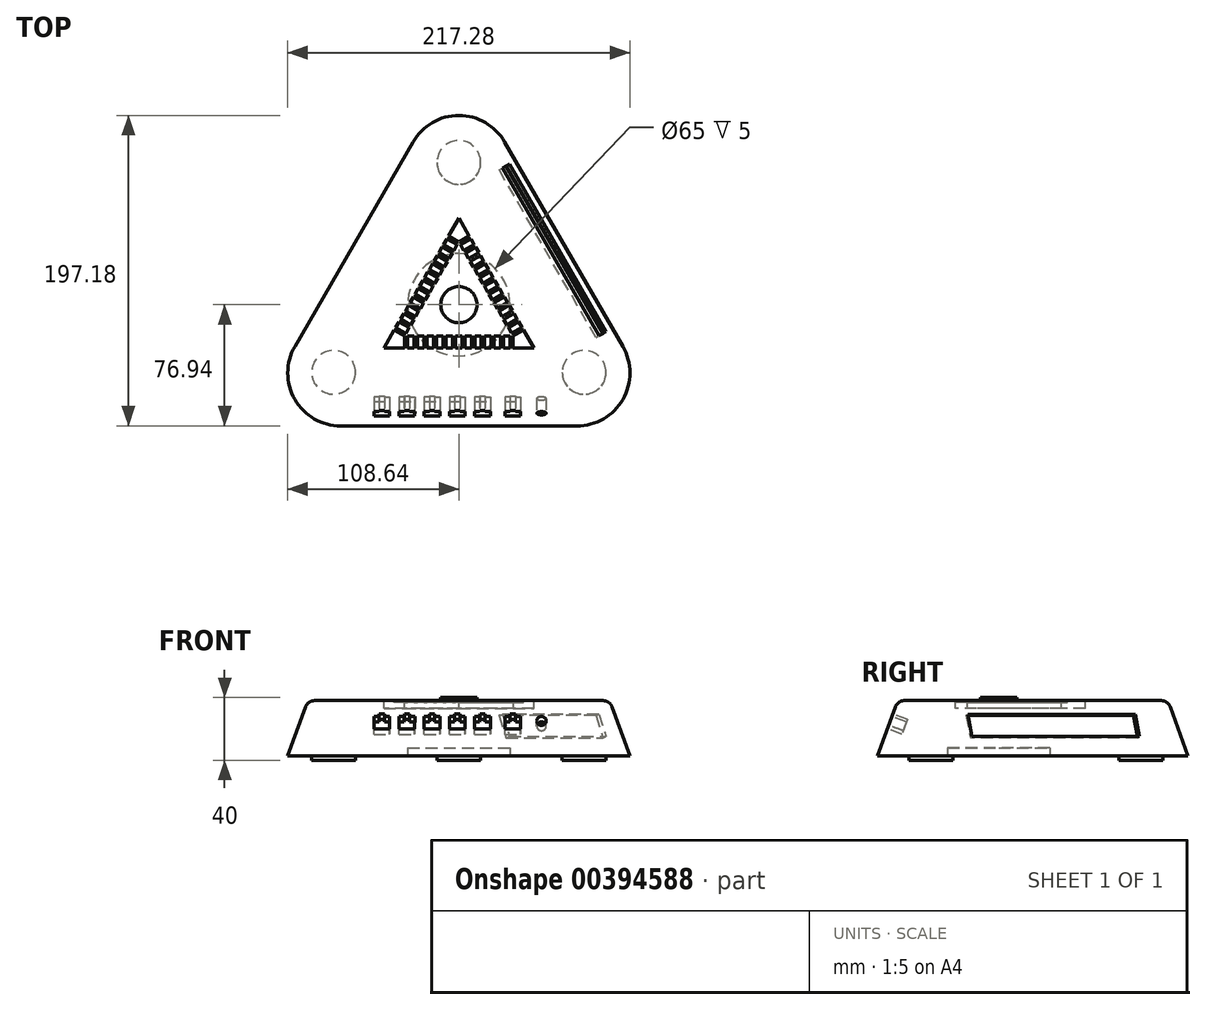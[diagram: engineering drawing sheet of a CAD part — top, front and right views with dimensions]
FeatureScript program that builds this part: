
annotation { "Feature Type Name" : "Feature", "Feature Type Description" : "" }
export const myFeature = defineFeature(function(context is Context, id is Id, definition is map)
    precondition{}
    {
        {
            var Q0;
            Q0=qCreatedBy(makeId("Top.planeOp"),FACE);
            var sketch = newSketch(context, id + "F0", { "sketchPlane" : qUnion([Q0])});
            skCircle(sketch, "E0.cCircle", {"center": v(0, 0) * mm, "radius": 73.3 * mm, "construction": true});
            skLineSegment(sketch, "E0.0", {"start": v(75, -73.3) * mm, "end": v(-75, -73.3) * mm});
            skLineSegment(sketch, "E0.1", {"start": v(-100.98, -28.3) * mm, "end": v(-25.98, 101.6) * mm});
            skLineSegment(sketch, "E0.2", {"start": v(25.98, 101.6) * mm, "end": v(100.98, -28.3) * mm});
            skPoint(sketch, "E0.0.midPoint", {"position": v(0, -73.3) * mm});
            skPoint(sketch, "E1.visualSharp", {"position": v(0, 146.6) * mm});
            skArc(sketch, "E1.filletArc", {"start": v(25.98, 101.6) * mm, "mid": v(0, 116.6) * mm, "end": v(-25.98, 101.6) * mm});
            skPoint(sketch, "E2.visualSharp", {"position": v(126.96, -73.3) * mm});
            skArc(sketch, "E2.filletArc", {"start": v(75, -73.3) * mm, "mid": v(100.98, -58.3) * mm, "end": v(100.98, -28.3) * mm});
            skPoint(sketch, "E3.visualSharp", {"position": v(-126.96, -73.3) * mm});
            skArc(sketch, "E3.filletArc", {"start": v(-100.98, -28.3) * mm, "mid": v(-100.98, -58.3) * mm, "end": v(-75, -73.3) * mm});
            skSolve(sketch);
        }
        {
            var Q0;
            Q0=makeQuery(id+"F0.imprint","IMPRINT",FACE,{"disambiguationData":[TD([[makeQuery(id+"F0.imprint","IMPRINT",EDGE,{"derivedFrom":sQuery(id+"F0.wireOp",EDGE,"E0.0")}),-1.0]])]});
            extrude(context, id + "F1", {"entities" : qUnion([Q0]), "depth" : 25 * mm, "hasDraft" : true, "draftAngle" : 20 * degree, "draftPullDirection" : true, "hasSecondDirection" : true, "secondDirectionOppositeDirection" : true, "secondDirectionDepth" : 10 * mm, "hasSecondDirectionDraft" : true, "secondDirectionDraftAngle" : 20 * degree});
        }
        {
            var Q0;
            Q0=makeQuery(id+"F1.opExtrude","CAP_EDGE",EDGE,{"disambiguationData":[OSD([sQuery(id+"F0.wireOp",EDGE,"E0.0")])],"isStart":false});
            var Q1;
            Q1=makeQuery(id+"F1.opExtrude","CAP_EDGE",EDGE,{"disambiguationData":[OSD([sQuery(id+"F0.wireOp",EDGE,"E0.2")])],"isStart":false});
            var Q2;
            Q2=makeQuery(id+"F1.opExtrude","CAP_EDGE",EDGE,{"disambiguationData":[OSD([sQuery(id+"F0.wireOp",EDGE,"E0.1")])],"isStart":false});
            fillet(context, id + "F2", {"entities" : qUnion([Q0, Q1, Q2]), "radius" : 6 * mm, "tangentPropagation" : true, "allowEdgeOverflow" : false});
        }
        {
            var Q0;
            Q0=makeQuery(id+"F1.opExtrude","CAP_FACE",FACE,{"disambiguationData":[OSD([sQuery(id+"F0.wireOp",EDGE,"E0.0"),sQuery(id+"F0.wireOp",EDGE,"E0.1"),sQuery(id+"F0.wireOp",EDGE,"E0.2"),sQuery(id+"F0.wireOp",EDGE,"E1.filletArc"),sQuery(id+"F0.wireOp",EDGE,"E2.filletArc"),sQuery(id+"F0.wireOp",EDGE,"E3.filletArc")])],"isStart":false});
            var sketch = newSketch(context, id + "F3", { "sketchPlane" : qUnion([Q0])});
            skCircle(sketch, "E4", {"center": v(0, 0) * mm, "radius": 11.5 * mm});
            skCircle(sketch, "E5.cCircle", {"center": v(0, 0) * mm, "radius": 20 * mm, "construction": true});
            skLineSegment(sketch, "E5.0", {"start": v(34.64, -20) * mm, "end": v(-34.64, -20) * mm});
            skLineSegment(sketch, "E5.1", {"start": v(-34.64, -20) * mm, "end": v(0, 40) * mm});
            skLineSegment(sketch, "E5.2", {"start": v(0, 40) * mm, "end": v(34.64, -20) * mm});
            skPoint(sketch, "E5.0.midPoint", {"position": v(0, -20) * mm});
            skCircle(sketch, "E6.cCircle", {"center": v(0, 0) * mm, "radius": 27.5 * mm, "construction": true});
            skLineSegment(sketch, "E6.0", {"start": v(47.63, -27.5) * mm, "end": v(-47.63, -27.5) * mm});
            skLineSegment(sketch, "E6.1", {"start": v(-47.63, -27.5) * mm, "end": v(0, 55) * mm});
            skLineSegment(sketch, "E6.2", {"start": v(0, 55) * mm, "end": v(47.63, -27.5) * mm});
            skPoint(sketch, "E6.0.midPoint", {"position": v(0, -27.5) * mm});
            skSolve(sketch);
        }
        {
            var Q0;
            Q0=makeQuery(id+"F3.imprint","IMPRINT",FACE,{"disambiguationData":[TD([[makeQuery(id+"F3.imprint","IMPRINT",EDGE,{"derivedFrom":sQuery(id+"F3.wireOp",EDGE,"E4")}),1.0]])]});
            extrude(context, id + "F4", {"entities" : qUnion([Q0]), "operationType" : NewBodyOperationType.ADD, "depth" : 2 * mm});
        }
        {
            var Q0;
            Q0=makeQuery(id+"F4.opExtrude","CAP_FACE",FACE,{"disambiguationData":[OSD([sQuery(id+"F3.wireOp",EDGE,"E4")])],"isStart":false});
            var sketch = newSketch(context, id + "F5", { "sketchPlane" : qUnion([Q0])});
            skSolve(sketch);
        }
        {
            var Q0;
            Q0=makeQuery(id+"F1.opExtrude","CAP_FACE",FACE,{"disambiguationData":[OSD([sQuery(id+"F0.wireOp",EDGE,"E0.0"),sQuery(id+"F0.wireOp",EDGE,"E0.1"),sQuery(id+"F0.wireOp",EDGE,"E0.2"),sQuery(id+"F0.wireOp",EDGE,"E1.filletArc"),sQuery(id+"F0.wireOp",EDGE,"E2.filletArc"),sQuery(id+"F0.wireOp",EDGE,"E3.filletArc")])],"isStart":true});
            var sketch = newSketch(context, id + "F6", { "sketchPlane" : qUnion([Q0])});
            skPoint(sketch, "E7.orphan", {"position": v(0, 0) * mm});
            skPoint(sketch, "E8.orphan", {"position": v(-104.13, 60.12) * mm});
            skPoint(sketch, "E9.end.orphan", {"position": v(0, -120.24) * mm});
            skCircle(sketch, "E10", {"center": v(-79.56, 42.91) * mm, "radius": 13.93 * mm});
            skLineSegment(sketch, "E11", {"start": v(0, 0) * mm, "end": v(66.63, -38.47) * mm});
            skCircle(sketch, "E12.MirrorC", {"center": v(79.56, 42.91) * mm, "radius": 13.93 * mm});
            skCircle(sketch, "E13.MirrorC", {"center": v(0, -90.36) * mm, "radius": 13.93 * mm});
            skPoint(sketch, "E14.end.orphan", {"position": v(-66.63, -38.47) * mm});
            skPoint(sketch, "E15.end.orphan", {"position": v(0, 76.94) * mm});
            skCircle(sketch, "E16.cCircle", {"center": v(0, 0) * mm, "radius": 30 * mm, "construction": true});
            skPoint(sketch, "E16.0.midPoint", {"position": v(0, 30) * mm});
            skSolve(sketch);
        }
        {
            var Q0;
            Q0=qSketchRegion(id+"F6",true);
            extrude(context, id + "F7", {"entities" : qUnion([Q0]), "operationType" : NewBodyOperationType.ADD, "depth" : 3 * mm});
        }
        {
            var Q0;
            Q0=makeQuery(id+"F1.opExtrude","CAP_FACE",FACE,{"disambiguationData":[OSD([sQuery(id+"F0.wireOp",EDGE,"E0.0"),sQuery(id+"F0.wireOp",EDGE,"E0.1"),sQuery(id+"F0.wireOp",EDGE,"E0.2"),sQuery(id+"F0.wireOp",EDGE,"E1.filletArc"),sQuery(id+"F0.wireOp",EDGE,"E2.filletArc"),sQuery(id+"F0.wireOp",EDGE,"E3.filletArc")])],"isStart":true});
            var sketch = newSketch(context, id + "F8", { "sketchPlane" : qUnion([Q0])});
            skCircle(sketch, "E17", {"center": v(0, 0) * mm, "radius": 32.5 * mm});
            skSolve(sketch);
        }
        {
            var Q0;
            Q0=qSketchRegion(id+"F8",true);
            extrude(context, id + "F9", {"entities" : qUnion([Q0]), "operationType" : NewBodyOperationType.REMOVE, "oppositeDirection" : true, "depth" : 5 * mm});
        }
        {
            var Q0;
            Q0=makeQuery(id+"F1.*.split.splitOp","SPLIT",FACE,{"derivedFrom":makeQuery(id+"F1.opExtrude","SWEPT_FACE",FACE,{"disambiguationData":[OSD([sQuery(id+"F0.wireOp",EDGE,"E0.0")])]})});
            var sketch = newSketch(context, id + "F10", { "sketchPlane" : qUnion([Q0])});
            skLineSegment(sketch, "E18.top", {"start": v(-53.99, -17.5) * mm, "end": v(-43.99, -17.5) * mm});
            skLineSegment(sketch, "E19", {"start": v(-53.99, -9.3) * mm, "end": v(-53.99, -17.5) * mm});
            skLineSegment(sketch, "E20", {"start": v(-43.96, -9.24) * mm, "end": v(-43.99, -17.5) * mm});
            skLineSegment(sketch, "E21", {"start": v(-50.6, -7.5) * mm, "end": v(-47.3, -7.5) * mm});
            skLineSegment(sketch, "E22", {"start": v(-50.6, -7.5) * mm, "end": v(-50.74, -9.3) * mm});
            skLineSegment(sketch, "E23", {"start": v(-50.74, -9.3) * mm, "end": v(-53.99, -9.3) * mm});
            skLineSegment(sketch, "E24", {"start": v(-47.3, -7.5) * mm, "end": v(-47.3, -9.3) * mm});
            skLineSegment(sketch, "E25", {"start": v(-47.3, -9.3) * mm, "end": v(-43.96, -9.24) * mm});
            skPoint(sketch, "E18.left.start.orphan", {"position": v(-53.99, -7.5) * mm});
            skPoint(sketch, "E18.right.start.orphan", {"position": v(-43.99, -7.5) * mm});
            skLineSegment(sketch, "E26.1.0.0", {"start": v(-37.99, -9.3) * mm, "end": v(-37.99, -17.5) * mm});
            skLineSegment(sketch, "E26.1.0.1", {"start": v(-27.96, -9.24) * mm, "end": v(-27.99, -17.5) * mm});
            skPoint(sketch, "E26.1.0.2", {"position": v(-37.99, -7.5) * mm});
            skPoint(sketch, "E26.1.0.3", {"position": v(-27.99, -7.5) * mm});
            skLineSegment(sketch, "E26.1.0.4", {"start": v(-37.99, -17.5) * mm, "end": v(-27.99, -17.5) * mm});
            skLineSegment(sketch, "E26.1.0.5", {"start": v(-34.6, -7.5) * mm, "end": v(-31.3, -7.5) * mm});
            skLineSegment(sketch, "E26.1.0.6", {"start": v(-31.3, -7.5) * mm, "end": v(-31.3, -9.3) * mm});
            skLineSegment(sketch, "E26.1.0.7", {"start": v(-34.6, -7.5) * mm, "end": v(-34.74, -9.3) * mm});
            skLineSegment(sketch, "E26.1.0.8", {"start": v(-34.74, -9.3) * mm, "end": v(-37.99, -9.3) * mm});
            skLineSegment(sketch, "E26.1.0.9", {"start": v(-31.3, -9.3) * mm, "end": v(-27.96, -9.24) * mm});
            skLineSegment(sketch, "E26.2.0.0", {"start": v(-21.99, -9.3) * mm, "end": v(-21.99, -17.5) * mm});
            skLineSegment(sketch, "E26.2.0.1", {"start": v(-11.96, -9.24) * mm, "end": v(-11.99, -17.5) * mm});
            skPoint(sketch, "E26.2.0.2", {"position": v(-21.99, -7.5) * mm});
            skPoint(sketch, "E26.2.0.3", {"position": v(-11.99, -7.5) * mm});
            skLineSegment(sketch, "E26.2.0.4", {"start": v(-21.99, -17.5) * mm, "end": v(-11.99, -17.5) * mm});
            skLineSegment(sketch, "E26.2.0.5", {"start": v(-18.6, -7.5) * mm, "end": v(-15.3, -7.5) * mm});
            skLineSegment(sketch, "E26.2.0.6", {"start": v(-15.3, -7.5) * mm, "end": v(-15.3, -9.3) * mm});
            skLineSegment(sketch, "E26.2.0.7", {"start": v(-18.6, -7.5) * mm, "end": v(-18.74, -9.3) * mm});
            skLineSegment(sketch, "E26.2.0.8", {"start": v(-18.74, -9.3) * mm, "end": v(-21.99, -9.3) * mm});
            skLineSegment(sketch, "E26.2.0.9", {"start": v(-15.3, -9.3) * mm, "end": v(-11.96, -9.24) * mm});
            skLineSegment(sketch, "E26.3.0.0", {"start": v(-5.99, -9.3) * mm, "end": v(-5.99, -17.5) * mm});
            skLineSegment(sketch, "E26.3.0.1", {"start": v(4.04, -9.24) * mm, "end": v(4.01, -17.5) * mm});
            skPoint(sketch, "E26.3.0.2", {"position": v(-5.99, -7.5) * mm});
            skPoint(sketch, "E26.3.0.3", {"position": v(4.01, -7.5) * mm});
            skLineSegment(sketch, "E26.3.0.4", {"start": v(-5.99, -17.5) * mm, "end": v(4.01, -17.5) * mm});
            skLineSegment(sketch, "E26.3.0.5", {"start": v(-2.6, -7.5) * mm, "end": v(0.7, -7.5) * mm});
            skLineSegment(sketch, "E26.3.0.6", {"start": v(0.7, -7.5) * mm, "end": v(0.7, -9.3) * mm});
            skLineSegment(sketch, "E26.3.0.7", {"start": v(-2.6, -7.5) * mm, "end": v(-2.74, -9.3) * mm});
            skLineSegment(sketch, "E26.3.0.8", {"start": v(-2.74, -9.3) * mm, "end": v(-5.99, -9.3) * mm});
            skLineSegment(sketch, "E26.3.0.9", {"start": v(0.7, -9.3) * mm, "end": v(4.04, -9.24) * mm});
            skLineSegment(sketch, "E26.4.0.0", {"start": v(10.01, -9.3) * mm, "end": v(10.01, -17.5) * mm});
            skLineSegment(sketch, "E26.4.0.1", {"start": v(20.04, -9.24) * mm, "end": v(20.01, -17.5) * mm});
            skPoint(sketch, "E26.4.0.2", {"position": v(10.01, -7.5) * mm});
            skPoint(sketch, "E26.4.0.3", {"position": v(20.01, -7.5) * mm});
            skLineSegment(sketch, "E26.4.0.4", {"start": v(10.01, -17.5) * mm, "end": v(20.01, -17.5) * mm});
            skLineSegment(sketch, "E26.4.0.5", {"start": v(13.4, -7.5) * mm, "end": v(16.7, -7.5) * mm});
            skLineSegment(sketch, "E26.4.0.6", {"start": v(16.7, -7.5) * mm, "end": v(16.7, -9.3) * mm});
            skLineSegment(sketch, "E26.4.0.7", {"start": v(13.4, -7.5) * mm, "end": v(13.26, -9.3) * mm});
            skLineSegment(sketch, "E26.4.0.8", {"start": v(13.26, -9.3) * mm, "end": v(10.01, -9.3) * mm});
            skLineSegment(sketch, "E26.4.0.9", {"start": v(16.7, -9.3) * mm, "end": v(20.04, -9.24) * mm});
            skLineSegment(sketch, "E26.5.0.0", {"start": v(29.26, -9.3) * mm, "end": v(29.26, -17.5) * mm});
            skLineSegment(sketch, "E26.5.0.1", {"start": v(39.3, -9.24) * mm, "end": v(39.26, -17.5) * mm});
            skPoint(sketch, "E26.5.0.2", {"position": v(29.26, -7.5) * mm});
            skPoint(sketch, "E26.5.0.3", {"position": v(39.26, -7.5) * mm});
            skLineSegment(sketch, "E26.5.0.4", {"start": v(29.26, -17.5) * mm, "end": v(39.26, -17.5) * mm});
            skLineSegment(sketch, "E26.5.0.5", {"start": v(32.64, -7.5) * mm, "end": v(35.95, -7.5) * mm});
            skLineSegment(sketch, "E26.5.0.6", {"start": v(35.95, -7.5) * mm, "end": v(35.95, -9.3) * mm});
            skLineSegment(sketch, "E26.5.0.7", {"start": v(32.64, -7.5) * mm, "end": v(32.5, -9.3) * mm});
            skLineSegment(sketch, "E26.5.0.8", {"start": v(32.5, -9.3) * mm, "end": v(29.26, -9.3) * mm});
            skLineSegment(sketch, "E26.5.0.9", {"start": v(35.95, -9.3) * mm, "end": v(39.3, -9.24) * mm});
            skLineSegment(sketch, "E26.direction1", {"start": v(-53.99, -17.5) * mm, "end": v(-37.99, -17.5) * mm, "construction": true});
            skCircle(sketch, "E27", {"center": v(52.49, -12.2) * mm, "radius": 3 * mm});
            skSolve(sketch);
        }
        {
            var Q0;
            Q0=qSketchRegion(id+"F10",true);
            extrude(context, id + "F11", {"entities" : qUnion([Q0]), "operationType" : NewBodyOperationType.REMOVE, "oppositeDirection" : true, "depth" : 2 * mm});
        }
        {
            var Q0;
            Q0=qCreatedBy(makeId("Front.planeOp"),FACE);
            var sketch = newSketch(context, id + "F12", { "sketchPlane" : qUnion([Q0])});
            skLineSegment(sketch, "E28", {"start": v(0, 27.54) * mm, "end": v(0, -12.74) * mm});
            skSolve(sketch);
        }
        {
            var Q0;
            Q0=qSketchRegion(id+"F3",true);
            extrude(context, id + "F13", {"entities" : qUnion([Q0]), "operationType" : NewBodyOperationType.REMOVE, "oppositeDirection" : true, "depth" : 5 * mm});
        }
        {
            var Q0;
            Q0=makeQuery(id+"F13.boolean.opBoolean","SPLIT",FACE,{"disambiguationData":[TD([makeQuery(id+"F4.opExtrude","SWEPT_FACE",FACE,{"disambiguationData":[OSD([sQuery(id+"F3.wireOp",EDGE,"E4")])]})])],"derivedFrom":makeQuery(id+"F1.opExtrude","CAP_FACE",FACE,{"disambiguationData":[OSD([sQuery(id+"F0.wireOp",EDGE,"E0.0"),sQuery(id+"F0.wireOp",EDGE,"E0.1"),sQuery(id+"F0.wireOp",EDGE,"E0.2"),sQuery(id+"F0.wireOp",EDGE,"E1.filletArc"),sQuery(id+"F0.wireOp",EDGE,"E2.filletArc"),sQuery(id+"F0.wireOp",EDGE,"E3.filletArc")])],"isStart":false})});
            cPlane(context, id + "F14", {"entities" : qUnion([Q0]), "cplaneType" : CPlaneType.OFFSET, "offset" : 0 * mm, "oppositeDirection" : true, "width" : 150 * mm, "height" : 150 * mm});
        }
        {
            var Q0;
            Q0=qCreatedBy(id+"F14.planeOp",FACE);
            var sketch = newSketch(context, id + "F15", { "sketchPlane" : qUnion([Q0])});
            skLineSegment(sketch, "E29.bottom", {"start": v(-34.42, -19.8) * mm, "end": v(-32.44, -19.8) * mm});
            skLineSegment(sketch, "E29.top", {"start": v(-34.42, -28.4) * mm, "end": v(-32.44, -28.4) * mm});
            skLineSegment(sketch, "E29.left", {"start": v(-34.42, -19.8) * mm, "end": v(-34.42, -28.4) * mm});
            skLineSegment(sketch, "E29.right", {"start": v(-32.44, -19.8) * mm, "end": v(-32.44, -28.4) * mm});
            skLineSegment(sketch, "E30.1.0.0", {"start": v(-26.36, -19.8) * mm, "end": v(-26.36, -28.4) * mm});
            skLineSegment(sketch, "E30.1.0.1", {"start": v(-28.34, -19.8) * mm, "end": v(-28.34, -28.4) * mm});
            skLineSegment(sketch, "E30.1.0.2", {"start": v(-28.34, -28.4) * mm, "end": v(-26.36, -28.4) * mm});
            skLineSegment(sketch, "E30.1.0.3", {"start": v(-28.34, -19.8) * mm, "end": v(-26.36, -19.8) * mm});
            skLineSegment(sketch, "E30.2.0.0", {"start": v(-20.28, -19.8) * mm, "end": v(-20.28, -28.4) * mm});
            skLineSegment(sketch, "E30.2.0.1", {"start": v(-22.26, -19.8) * mm, "end": v(-22.26, -28.4) * mm});
            skLineSegment(sketch, "E30.2.0.2", {"start": v(-22.26, -28.4) * mm, "end": v(-20.28, -28.4) * mm});
            skLineSegment(sketch, "E30.2.0.3", {"start": v(-22.26, -19.8) * mm, "end": v(-20.28, -19.8) * mm});
            skLineSegment(sketch, "E30.3.0.0", {"start": v(-14.2, -19.8) * mm, "end": v(-14.2, -28.4) * mm});
            skLineSegment(sketch, "E30.3.0.1", {"start": v(-16.18, -19.8) * mm, "end": v(-16.18, -28.4) * mm});
            skLineSegment(sketch, "E30.3.0.2", {"start": v(-16.18, -28.4) * mm, "end": v(-14.2, -28.4) * mm});
            skLineSegment(sketch, "E30.3.0.3", {"start": v(-16.18, -19.8) * mm, "end": v(-14.2, -19.8) * mm});
            skLineSegment(sketch, "E30.4.0.0", {"start": v(-8.12, -19.8) * mm, "end": v(-8.12, -28.4) * mm});
            skLineSegment(sketch, "E30.4.0.1", {"start": v(-10.1, -19.8) * mm, "end": v(-10.1, -28.4) * mm});
            skLineSegment(sketch, "E30.4.0.2", {"start": v(-10.1, -28.4) * mm, "end": v(-8.12, -28.4) * mm});
            skLineSegment(sketch, "E30.4.0.3", {"start": v(-10.1, -19.8) * mm, "end": v(-8.12, -19.8) * mm});
            skLineSegment(sketch, "E30.5.0.0", {"start": v(-2.04, -19.8) * mm, "end": v(-2.04, -28.4) * mm});
            skLineSegment(sketch, "E30.5.0.1", {"start": v(-4.02, -19.8) * mm, "end": v(-4.02, -28.4) * mm});
            skLineSegment(sketch, "E30.5.0.2", {"start": v(-4.02, -28.4) * mm, "end": v(-2.04, -28.4) * mm});
            skLineSegment(sketch, "E30.5.0.3", {"start": v(-4.02, -19.8) * mm, "end": v(-2.04, -19.8) * mm});
            skLineSegment(sketch, "E30.6.0.0", {"start": v(4.04, -19.8) * mm, "end": v(4.04, -28.4) * mm});
            skLineSegment(sketch, "E30.6.0.1", {"start": v(2.06, -19.8) * mm, "end": v(2.06, -28.4) * mm});
            skLineSegment(sketch, "E30.6.0.2", {"start": v(2.06, -28.4) * mm, "end": v(4.04, -28.4) * mm});
            skLineSegment(sketch, "E30.6.0.3", {"start": v(2.06, -19.8) * mm, "end": v(4.04, -19.8) * mm});
            skLineSegment(sketch, "E30.7.0.0", {"start": v(10.12, -19.8) * mm, "end": v(10.12, -28.4) * mm});
            skLineSegment(sketch, "E30.7.0.1", {"start": v(8.14, -19.8) * mm, "end": v(8.14, -28.4) * mm});
            skLineSegment(sketch, "E30.7.0.2", {"start": v(8.14, -28.4) * mm, "end": v(10.12, -28.4) * mm});
            skLineSegment(sketch, "E30.7.0.3", {"start": v(8.14, -19.8) * mm, "end": v(10.12, -19.8) * mm});
            skLineSegment(sketch, "E30.8.0.0", {"start": v(16.2, -19.8) * mm, "end": v(16.2, -28.4) * mm});
            skLineSegment(sketch, "E30.8.0.1", {"start": v(14.22, -19.8) * mm, "end": v(14.22, -28.4) * mm});
            skLineSegment(sketch, "E30.8.0.2", {"start": v(14.22, -28.4) * mm, "end": v(16.2, -28.4) * mm});
            skLineSegment(sketch, "E30.8.0.3", {"start": v(14.22, -19.8) * mm, "end": v(16.2, -19.8) * mm});
            skLineSegment(sketch, "E30.9.0.0", {"start": v(22.28, -19.8) * mm, "end": v(22.28, -28.4) * mm});
            skLineSegment(sketch, "E30.9.0.1", {"start": v(20.3, -19.8) * mm, "end": v(20.3, -28.4) * mm});
            skLineSegment(sketch, "E30.9.0.2", {"start": v(20.3, -28.4) * mm, "end": v(22.28, -28.4) * mm});
            skLineSegment(sketch, "E30.9.0.3", {"start": v(20.3, -19.8) * mm, "end": v(22.28, -19.8) * mm});
            skLineSegment(sketch, "E30.10.0.0", {"start": v(28.36, -19.8) * mm, "end": v(28.36, -28.4) * mm});
            skLineSegment(sketch, "E30.10.0.1", {"start": v(26.38, -19.8) * mm, "end": v(26.38, -28.4) * mm});
            skLineSegment(sketch, "E30.10.0.2", {"start": v(26.38, -28.4) * mm, "end": v(28.36, -28.4) * mm});
            skLineSegment(sketch, "E30.10.0.3", {"start": v(26.38, -19.8) * mm, "end": v(28.36, -19.8) * mm});
            skLineSegment(sketch, "E30.11.0.0", {"start": v(34.44, -19.8) * mm, "end": v(34.44, -28.4) * mm});
            skLineSegment(sketch, "E30.11.0.1", {"start": v(32.46, -19.8) * mm, "end": v(32.46, -28.4) * mm});
            skLineSegment(sketch, "E30.11.0.2", {"start": v(32.46, -28.4) * mm, "end": v(34.44, -28.4) * mm});
            skLineSegment(sketch, "E30.11.0.3", {"start": v(32.46, -19.8) * mm, "end": v(34.44, -19.8) * mm});
            skLineSegment(sketch, "E30.direction1", {"start": v(-34.42, -28.4) * mm, "end": v(-28.34, -28.4) * mm, "construction": true});
            skLineSegment(sketch, "E31.1.0", {"start": v(18.16, 8.13) * mm, "end": v(25.6, 12.43) * mm});
            skLineSegment(sketch, "E31.1.1", {"start": v(15.12, 13.4) * mm, "end": v(22.57, 17.7) * mm});
            skLineSegment(sketch, "E31.1.2", {"start": v(2.96, 34.46) * mm, "end": v(10.4, 38.76) * mm});
            skLineSegment(sketch, "E31.1.3", {"start": v(12.08, 18.66) * mm, "end": v(19.53, 22.97) * mm});
            skLineSegment(sketch, "E31.1.4", {"start": v(-0.08, 39.73) * mm, "end": v(7.37, 44.03) * mm});
            skLineSegment(sketch, "E31.1.5", {"start": v(10.03, 22.21) * mm, "end": v(17.48, 26.52) * mm});
            skLineSegment(sketch, "E31.1.6", {"start": v(24.24, -2.4) * mm, "end": v(31.69, 1.9) * mm});
            skLineSegment(sketch, "E31.1.7", {"start": v(28.27, -9.38) * mm, "end": v(35.72, -5.08) * mm});
            skLineSegment(sketch, "E31.1.8", {"start": v(27.28, -7.66) * mm, "end": v(34.73, -3.36) * mm});
            skLineSegment(sketch, "E31.1.9", {"start": v(31.3, -14.64) * mm, "end": v(38.76, -10.34) * mm});
            skLineSegment(sketch, "E31.1.10", {"start": v(30.32, -12.93) * mm, "end": v(37.77, -8.63) * mm});
            skLineSegment(sketch, "E31.1.11", {"start": v(33.36, -18.2) * mm, "end": v(40.8, -13.9) * mm});
            skLineSegment(sketch, "E31.1.12", {"start": v(34.35, -19.9) * mm, "end": v(41.8, -15.6) * mm});
            skLineSegment(sketch, "E31.1.13", {"start": v(22.19, 1.15) * mm, "end": v(29.64, 5.45) * mm});
            skLineSegment(sketch, "E31.1.14", {"start": v(6.99, 27.48) * mm, "end": v(14.44, 31.78) * mm});
            skLineSegment(sketch, "E31.1.15", {"start": v(19.15, 6.42) * mm, "end": v(26.6, 10.72) * mm});
            skLineSegment(sketch, "E31.1.16", {"start": v(25.23, -4.11) * mm, "end": v(32.68, 0.19) * mm});
            skLineSegment(sketch, "E31.1.17", {"start": v(9.04, 23.93) * mm, "end": v(16.49, 28.23) * mm});
            skLineSegment(sketch, "E31.1.18", {"start": v(21.2, 2.87) * mm, "end": v(28.65, 7.17) * mm});
            skLineSegment(sketch, "E31.1.19", {"start": v(6, 29.2) * mm, "end": v(13.45, 33.5) * mm});
            skLineSegment(sketch, "E31.1.20", {"start": v(13.07, 16.95) * mm, "end": v(20.52, 21.25) * mm});
            skLineSegment(sketch, "E31.1.21", {"start": v(0.9, 38.01) * mm, "end": v(8.36, 42.31) * mm});
            skLineSegment(sketch, "E31.1.22", {"start": v(3.95, 32.75) * mm, "end": v(11.4, 37.05) * mm});
            skLineSegment(sketch, "E31.1.23", {"start": v(16.1, 11.68) * mm, "end": v(23.56, 15.99) * mm});
            skLineSegment(sketch, "E31.1.24", {"start": v(34.35, -19.9) * mm, "end": v(33.36, -18.2) * mm});
            skLineSegment(sketch, "E31.1.25", {"start": v(17.48, 26.52) * mm, "end": v(16.49, 28.23) * mm});
            skLineSegment(sketch, "E31.1.26", {"start": v(29.64, 5.45) * mm, "end": v(28.65, 7.17) * mm});
            skLineSegment(sketch, "E31.1.27", {"start": v(14.44, 31.78) * mm, "end": v(13.45, 33.5) * mm});
            skLineSegment(sketch, "E31.1.28", {"start": v(13.07, 16.95) * mm, "end": v(12.08, 18.66) * mm});
            skLineSegment(sketch, "E31.1.29", {"start": v(0.9, 38.01) * mm, "end": v(-0.08, 39.73) * mm});
            skLineSegment(sketch, "E31.1.30", {"start": v(26.6, 10.72) * mm, "end": v(25.6, 12.43) * mm});
            skLineSegment(sketch, "E31.1.31", {"start": v(28.27, -9.38) * mm, "end": v(27.28, -7.66) * mm});
            skLineSegment(sketch, "E31.1.32", {"start": v(31.3, -14.64) * mm, "end": v(30.32, -12.93) * mm});
            skLineSegment(sketch, "E31.1.33", {"start": v(38.76, -10.34) * mm, "end": v(37.77, -8.63) * mm});
            skLineSegment(sketch, "E31.1.34", {"start": v(41.8, -15.6) * mm, "end": v(40.8, -13.9) * mm});
            skLineSegment(sketch, "E31.1.35", {"start": v(25.23, -4.11) * mm, "end": v(24.24, -2.4) * mm});
            skLineSegment(sketch, "E31.1.36", {"start": v(20.52, 21.25) * mm, "end": v(19.53, 22.97) * mm});
            skLineSegment(sketch, "E31.1.37", {"start": v(8.36, 42.31) * mm, "end": v(7.37, 44.03) * mm});
            skLineSegment(sketch, "E31.1.38", {"start": v(32.68, 0.19) * mm, "end": v(31.69, 1.9) * mm});
            skLineSegment(sketch, "E31.1.39", {"start": v(16.1, 11.68) * mm, "end": v(15.12, 13.4) * mm});
            skLineSegment(sketch, "E31.1.40", {"start": v(3.95, 32.75) * mm, "end": v(2.96, 34.46) * mm});
            skLineSegment(sketch, "E31.1.41", {"start": v(41.8, -15.6) * mm, "end": v(38.76, -10.34) * mm, "construction": true});
            skLineSegment(sketch, "E31.1.42", {"start": v(19.15, 6.42) * mm, "end": v(18.16, 8.13) * mm});
            skLineSegment(sketch, "E31.1.43", {"start": v(6.99, 27.48) * mm, "end": v(6, 29.2) * mm});
            skLineSegment(sketch, "E31.1.44", {"start": v(23.56, 15.99) * mm, "end": v(22.57, 17.7) * mm});
            skLineSegment(sketch, "E31.1.45", {"start": v(11.4, 37.05) * mm, "end": v(10.4, 38.76) * mm});
            skLineSegment(sketch, "E31.1.46", {"start": v(22.19, 1.15) * mm, "end": v(21.2, 2.87) * mm});
            skLineSegment(sketch, "E31.1.47", {"start": v(10.03, 22.21) * mm, "end": v(9.04, 23.93) * mm});
            skLineSegment(sketch, "E31.1.48", {"start": v(35.72, -5.08) * mm, "end": v(34.73, -3.36) * mm});
            skLineSegment(sketch, "E31.2.0", {"start": v(-16.12, 11.66) * mm, "end": v(-23.57, 15.96) * mm});
            skLineSegment(sketch, "E31.2.1", {"start": v(-19.16, 6.4) * mm, "end": v(-26.61, 10.7) * mm});
            skLineSegment(sketch, "E31.2.2", {"start": v(-31.32, -14.67) * mm, "end": v(-38.77, -10.37) * mm});
            skLineSegment(sketch, "E31.2.3", {"start": v(-22.2, 1.13) * mm, "end": v(-29.65, 5.43) * mm});
            skLineSegment(sketch, "E31.2.4", {"start": v(-34.36, -19.93) * mm, "end": v(-41.81, -15.63) * mm});
            skLineSegment(sketch, "E31.2.5", {"start": v(-24.25, -2.42) * mm, "end": v(-31.7, 1.88) * mm});
            skLineSegment(sketch, "E31.2.6", {"start": v(-10.04, 22.2) * mm, "end": v(-17.5, 26.5) * mm});
            skLineSegment(sketch, "E31.2.7", {"start": v(-6.01, 29.17) * mm, "end": v(-13.46, 33.47) * mm});
            skLineSegment(sketch, "E31.2.8", {"start": v(-7, 27.46) * mm, "end": v(-14.45, 31.76) * mm});
            skLineSegment(sketch, "E31.2.9", {"start": v(-2.97, 34.44) * mm, "end": v(-10.42, 38.74) * mm});
            skLineSegment(sketch, "E31.2.10", {"start": v(-3.96, 32.72) * mm, "end": v(-11.41, 37.02) * mm});
            skLineSegment(sketch, "E31.2.11", {"start": v(-0.92, 37.99) * mm, "end": v(-8.37, 42.29) * mm});
            skLineSegment(sketch, "E31.2.12", {"start": v(0.07, 39.7) * mm, "end": v(-7.38, 44) * mm});
            skLineSegment(sketch, "E31.2.13", {"start": v(-12.1, 18.64) * mm, "end": v(-19.54, 22.94) * mm});
            skLineSegment(sketch, "E31.2.14", {"start": v(-27.3, -7.69) * mm, "end": v(-34.74, -3.39) * mm});
            skLineSegment(sketch, "E31.2.15", {"start": v(-15.13, 13.37) * mm, "end": v(-22.58, 17.68) * mm});
            skLineSegment(sketch, "E31.2.16", {"start": v(-9.05, 23.9) * mm, "end": v(-16.5, 28.2) * mm});
            skLineSegment(sketch, "E31.2.17", {"start": v(-25.24, -4.14) * mm, "end": v(-32.7, 0.16) * mm});
            skLineSegment(sketch, "E31.2.18", {"start": v(-13.08, 16.92) * mm, "end": v(-20.53, 21.23) * mm});
            skLineSegment(sketch, "E31.2.19", {"start": v(-28.28, -9.4) * mm, "end": v(-35.73, -5.1) * mm});
            skLineSegment(sketch, "E31.2.20", {"start": v(-21.21, 2.84) * mm, "end": v(-28.66, 7.14) * mm});
            skLineSegment(sketch, "E31.2.21", {"start": v(-33.37, -18.22) * mm, "end": v(-40.82, -13.92) * mm});
            skLineSegment(sketch, "E31.2.22", {"start": v(-30.33, -12.95) * mm, "end": v(-37.78, -8.65) * mm});
            skLineSegment(sketch, "E31.2.23", {"start": v(-18.17, 8.1) * mm, "end": v(-25.62, 12.4) * mm});
            skLineSegment(sketch, "E31.2.24", {"start": v(0.07, 39.7) * mm, "end": v(-0.92, 37.99) * mm});
            skLineSegment(sketch, "E31.2.25", {"start": v(-31.7, 1.88) * mm, "end": v(-32.7, 0.16) * mm});
            skLineSegment(sketch, "E31.2.26", {"start": v(-19.54, 22.94) * mm, "end": v(-20.53, 21.23) * mm});
            skLineSegment(sketch, "E31.2.27", {"start": v(-34.74, -3.39) * mm, "end": v(-35.73, -5.1) * mm});
            skLineSegment(sketch, "E31.2.28", {"start": v(-21.21, 2.84) * mm, "end": v(-22.2, 1.13) * mm});
            skLineSegment(sketch, "E31.2.29", {"start": v(-33.37, -18.22) * mm, "end": v(-34.36, -19.93) * mm});
            skLineSegment(sketch, "E31.2.30", {"start": v(-22.58, 17.68) * mm, "end": v(-23.57, 15.96) * mm});
            skLineSegment(sketch, "E31.2.31", {"start": v(-6.01, 29.17) * mm, "end": v(-7, 27.46) * mm});
            skLineSegment(sketch, "E31.2.32", {"start": v(-2.97, 34.44) * mm, "end": v(-3.96, 32.72) * mm});
            skLineSegment(sketch, "E31.2.33", {"start": v(-10.42, 38.74) * mm, "end": v(-11.41, 37.02) * mm});
            skLineSegment(sketch, "E31.2.34", {"start": v(-7.38, 44) * mm, "end": v(-8.37, 42.29) * mm});
            skLineSegment(sketch, "E31.2.35", {"start": v(-9.05, 23.9) * mm, "end": v(-10.04, 22.2) * mm});
            skLineSegment(sketch, "E31.2.36", {"start": v(-28.66, 7.14) * mm, "end": v(-29.65, 5.43) * mm});
            skLineSegment(sketch, "E31.2.37", {"start": v(-40.82, -13.92) * mm, "end": v(-41.81, -15.63) * mm});
            skLineSegment(sketch, "E31.2.38", {"start": v(-16.5, 28.2) * mm, "end": v(-17.5, 26.5) * mm});
            skLineSegment(sketch, "E31.2.39", {"start": v(-18.17, 8.1) * mm, "end": v(-19.16, 6.4) * mm});
            skLineSegment(sketch, "E31.2.40", {"start": v(-30.33, -12.95) * mm, "end": v(-31.32, -14.67) * mm});
            skLineSegment(sketch, "E31.2.41", {"start": v(-7.38, 44) * mm, "end": v(-10.42, 38.74) * mm, "construction": true});
            skLineSegment(sketch, "E31.2.42", {"start": v(-15.13, 13.37) * mm, "end": v(-16.12, 11.66) * mm});
            skLineSegment(sketch, "E31.2.43", {"start": v(-27.3, -7.69) * mm, "end": v(-28.28, -9.4) * mm});
            skLineSegment(sketch, "E31.2.44", {"start": v(-25.62, 12.4) * mm, "end": v(-26.61, 10.7) * mm});
            skLineSegment(sketch, "E31.2.45", {"start": v(-37.78, -8.65) * mm, "end": v(-38.77, -10.37) * mm});
            skLineSegment(sketch, "E31.2.46", {"start": v(-12.1, 18.64) * mm, "end": v(-13.08, 16.92) * mm});
            skLineSegment(sketch, "E31.2.47", {"start": v(-24.25, -2.42) * mm, "end": v(-25.24, -4.14) * mm});
            skLineSegment(sketch, "E31.2.48", {"start": v(-13.46, 33.47) * mm, "end": v(-14.45, 31.76) * mm});
            skPoint(sketch, "E31.center", {"position": v(0, 0) * mm});
            skSolve(sketch);
        }
        {
            var Q0;
            Q0=qSketchRegion(id+"F15",true);
            extrude(context, id + "F16", {"entities" : qUnion([Q0]), "operationType" : NewBodyOperationType.ADD, "oppositeDirection" : true, "depth" : 1 * mm});
        }
        {
            var Q0;
            Q0=qSketchRegion(id+"F10",true);
            extrude(context, id + "F17", {"entities" : qUnion([Q0]), "operationType" : NewBodyOperationType.REMOVE, "oppositeDirection" : true, "depth" : 10 * mm});
        }
        {
            var Q0;
            Q0=makeQuery(id+"F1.*.split.splitOp","SPLIT",FACE,{"derivedFrom":makeQuery(id+"F1.opExtrude","SWEPT_FACE",FACE,{"disambiguationData":[OSD([sQuery(id+"F0.wireOp",EDGE,"E0.2")])]})});
            var sketch = newSketch(context, id + "F18", { "sketchPlane" : qUnion([Q0])});
            skLineSegment(sketch, "E32", {"start": v(-58.76, -19.42) * mm, "end": v(61.73, 4.37) * mm});
            skLineSegment(sketch, "E33", {"start": v(64.63, -10.34) * mm, "end": v(-55.85, -34.13) * mm});
            skLineSegment(sketch, "E34", {"start": v(-58.76, -19.42) * mm, "end": v(-55.85, -34.13) * mm});
            skLineSegment(sketch, "E35.MirrorCS", {"start": v(61.73, 4.37) * mm, "end": v(64.63, -10.34) * mm});
            skSolve(sketch);
        }
        {
            var Q0;
            Q0=qSketchRegion(id+"F18",true);
            var Q1;
            Q1=makeQuery(id+"F1.*.split.splitOp","SPLIT",FACE,{"derivedFrom":makeQuery(id+"F1.opExtrude","SWEPT_FACE",FACE,{"disambiguationData":[OSD([sQuery(id+"F0.wireOp",EDGE,"E0.0")])]})});
            extrude(context, id + "F19", {"entities" : qUnion([Q0]), "operationType" : NewBodyOperationType.REMOVE, "oppositeDirection" : true, "endBoundEntityFace" : qUnion([Q1]), "depth" : 2.5 * mm});
        }
    });
